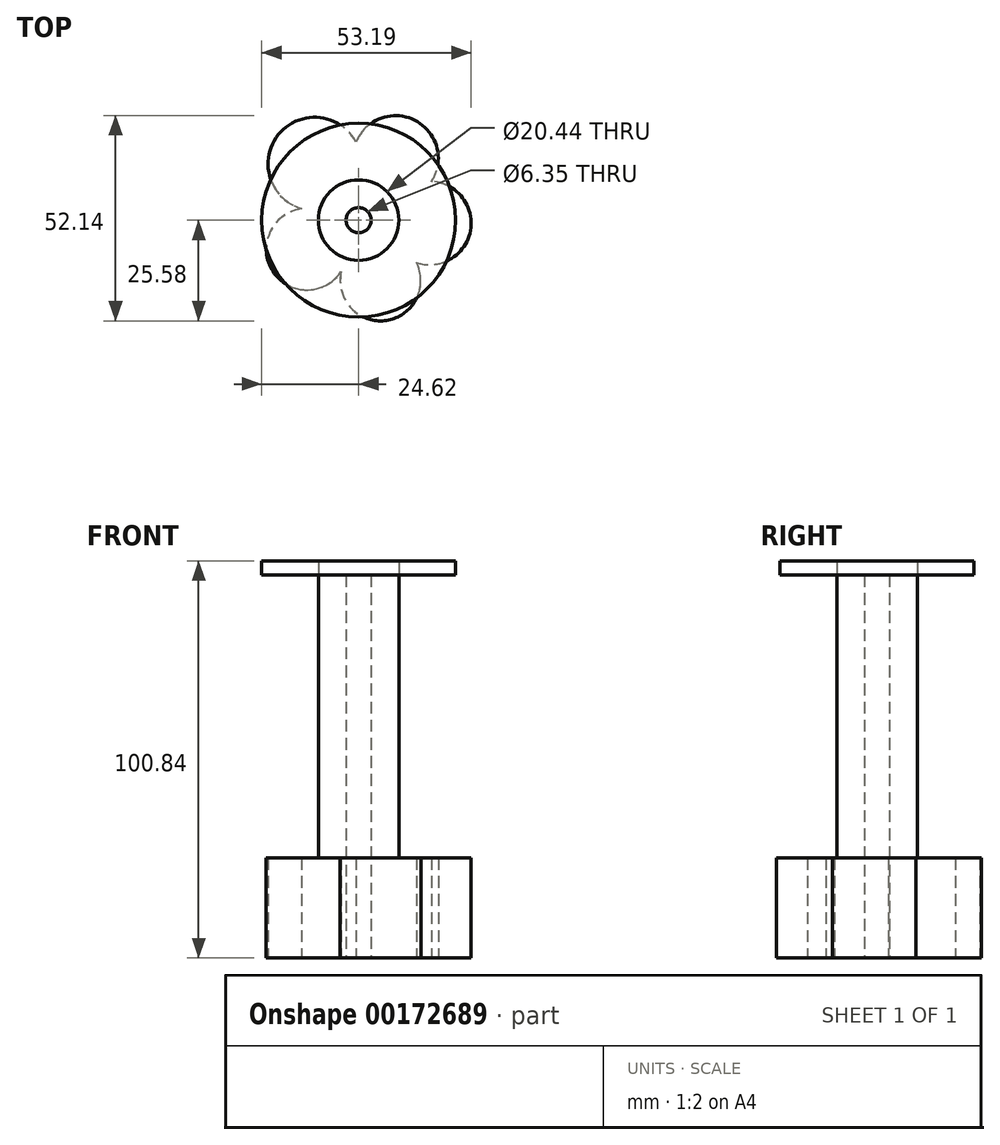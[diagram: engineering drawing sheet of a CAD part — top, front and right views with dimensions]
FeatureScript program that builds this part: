
annotation { "Feature Type Name" : "Feature", "Feature Type Description" : "" }
export const myFeature = defineFeature(function(context is Context, id is Id, definition is map)
    precondition{}
    {
        {
            var Q0;
            Q0=qCreatedBy(makeId("Top.planeOp"),FACE);
            var sketch = newSketch(context, id + "F0", { "sketchPlane" : qUnion([Q0])});
            skCircle(sketch, "E0", {"center": v(0, 0) * mm, "radius": 10.22 * mm});
            skArc(sketch, "E1", {"start": v(-0.66, 19.85) * mm, "mid": v(-20.34, 21.8) * mm, "end": v(-14.47, 2.9) * mm});
            skArc(sketch, "E2", {"start": v(-14.47, 2.9) * mm, "mid": v(-21.85, -12.9) * mm, "end": v(-4.4, -13) * mm});
            skArc(sketch, "E3", {"start": v(-4.4, -13) * mm, "mid": v(6.71, -25.51) * mm, "end": v(14.72, -10.8) * mm});
            skArc(sketch, "E4", {"start": v(18.51, 9.83) * mm, "mid": v(14.41, 25.32) * mm, "end": v(-0.66, 19.85) * mm});
            skArc(sketch, "E5", {"start": v(14.72, -10.8) * mm, "mid": v(28.4, -2.65) * mm, "end": v(18.51, 9.83) * mm});
            skPoint(sketch, "E6.orphan", {"position": v(0, 10.22) * mm});
            skSolve(sketch);
        }
        {
            var Q0;
            Q0=makeQuery(id+"F0.imprint","IMPRINT",FACE,{"disambiguationData":[TD([[makeQuery(id+"F0.imprint","IMPRINT",EDGE,{"derivedFrom":sQuery(id+"F0.wireOp",EDGE,"E0")}),-1.0]])]});
            extrude(context, id + "F1", {"entities" : qUnion([Q0]), "depth" : 25.4 * mm});
        }
        {
            var Q0;
            Q0=qCreatedBy(makeId("Top.planeOp"),FACE);
            var sketch = newSketch(context, id + "F2", { "sketchPlane" : qUnion([Q0])});
            skCircle(sketch, "E7", {"center": v(0, 0) * mm, "radius": 10.22 * mm});
            skSolve(sketch);
        }
        {
            var Q0;
            Q0=makeQuery(id+"F2.imprint","IMPRINT",FACE,{"disambiguationData":[TD([[makeQuery(id+"F2.imprint","IMPRINT",EDGE,{"derivedFrom":sQuery(id+"F2.wireOp",EDGE,"E7")}),1.0]])]});
            extrude(context, id + "F3", {"entities" : qUnion([Q0]), "operationType" : NewBodyOperationType.ADD, "depth" : 7.62 * mm});
        }
        {
            var Q0;
            Q0=qCreatedBy(makeId("Top.planeOp"),FACE);
            var sketch = newSketch(context, id + "F4", { "sketchPlane" : qUnion([Q0])});
            skCircle(sketch, "E8", {"center": v(0, 0) * mm, "radius": 7.9 * mm});
            skSolve(sketch);
        }
        {
            var Q0;
            Q0=makeQuery(id+"F3.opExtrude","CAP_FACE",FACE,{"disambiguationData":[OSD([sQuery(id+"F2.wireOp",EDGE,"E7")])],"isStart":false});
            extrude(context, id + "F5", {"entities" : qUnion([Q0]), "operationType" : NewBodyOperationType.ADD, "depth" : 89.66 * mm});
        }
        {
            var Q0;
            Q0=makeQuery(id+"F5.opExtrude","CAP_FACE",FACE,{"disambiguationData":[OSD([sQuery(id+"F2.wireOp",EDGE,"E7")])],"isStart":false});
            var sketch = newSketch(context, id + "F6", { "sketchPlane" : qUnion([Q0])});
            skCircle(sketch, "E9", {"center": v(0, 0) * mm, "radius": 24.62 * mm});
            skSolve(sketch);
        }
        {
            var Q0;
            Q0=makeQuery(id+"F6.imprint","IMPRINT",FACE,{"disambiguationData":[TD([[makeQuery(id+"F6.imprint","IMPRINT",EDGE,{"derivedFrom":sQuery(id+"F6.wireOp",EDGE,"E9")}),1.0]])]});
            extrude(context, id + "F7", {"entities" : qUnion([Q0]), "depth" : 3.56 * mm});
        }
        {
            var Q0;
            Q0=sQuery(id+"F4.wireOp",VERTEX,"E8.center");
            var Q1;
            Q1=makeQuery(id+"F1.opExtrude","SWEPT_BODY",BODY,{"disambiguationData":[OSD([sQuery(id+"F0.wireOp",EDGE,"E0"),sQuery(id+"F0.wireOp",EDGE,"E1"),sQuery(id+"F0.wireOp",EDGE,"E2"),sQuery(id+"F0.wireOp",EDGE,"E3"),sQuery(id+"F0.wireOp",EDGE,"E4"),sQuery(id+"F0.wireOp",EDGE,"E5")])]});
            hole(context, id + "F8", {"style" : HoleStyle.SIMPLE, "endStyle" : HoleEndStyle.THROUGH, "oppositeDirection" : true, "holeDiameter" : 6.35 * mm, "locations" : qUnion([Q0]), "scope" : qUnion([Q1]), "isTappedThrough" : true});
        }
    });
